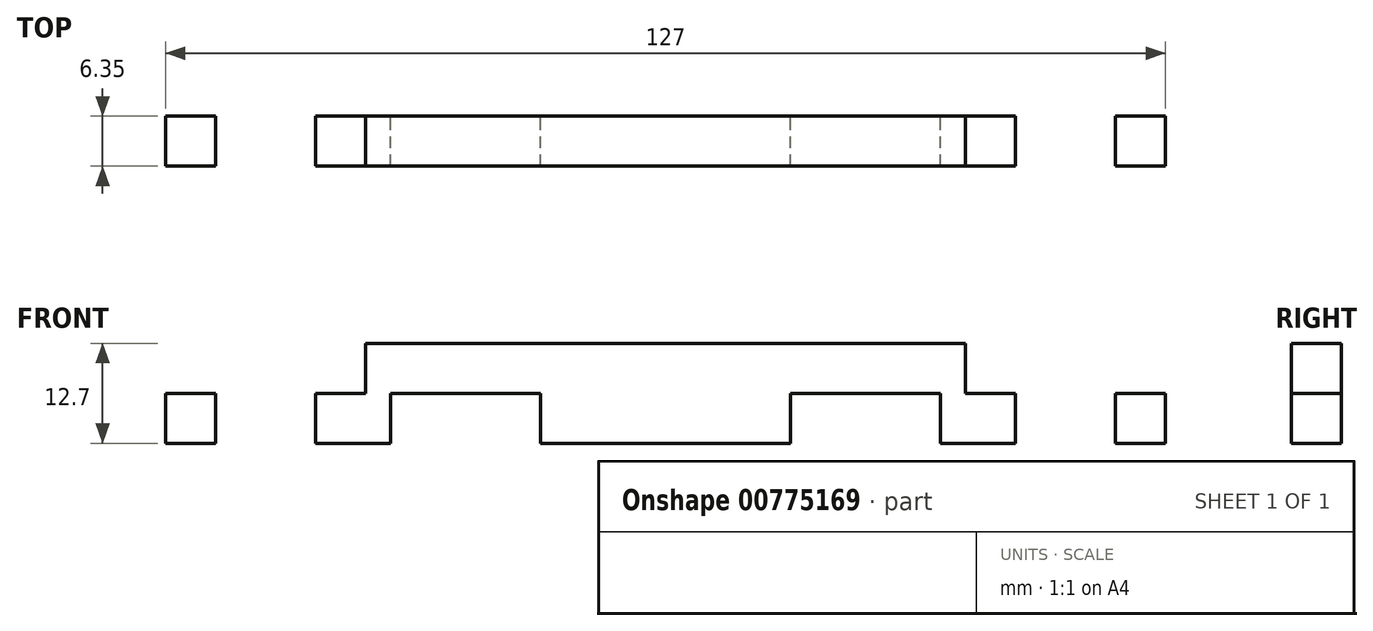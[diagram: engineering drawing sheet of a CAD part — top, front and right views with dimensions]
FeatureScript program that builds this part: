
annotation { "Feature Type Name" : "Feature", "Feature Type Description" : "" }
export const myFeature = defineFeature(function(context is Context, id is Id, definition is map)
    precondition{}
    {
        {
            var Q0;
            Q0=qCreatedBy(makeId("Front.planeOp"),FACE);
            var sketch = newSketch(context, id + "F0", { "sketchPlane" : qUnion([Q0])});
            skLineSegment(sketch, "E0.bottom", {"start": v(63.5, 9.52) * mm, "end": v(-63.5, 9.52) * mm});
            skLineSegment(sketch, "E0.top", {"start": v(63.5, -9.52) * mm, "end": v(-63.5, -9.53) * mm});
            skLineSegment(sketch, "E0.left", {"start": v(63.5, 9.53) * mm, "end": v(63.5, -9.52) * mm});
            skLineSegment(sketch, "E0.right", {"start": v(-63.5, 9.52) * mm, "end": v(-63.5, -9.53) * mm});
            skPoint(sketch, "E0.middle", {"position": v(0, 0) * mm});
            skLineSegment(sketch, "E1.bottom", {"start": v(-63.5, 9.52) * mm, "end": v(-57.15, 9.52) * mm});
            skLineSegment(sketch, "E1.top", {"start": v(-63.5, -9.53) * mm, "end": v(-57.15, -9.53) * mm});
            skLineSegment(sketch, "E1.right", {"start": v(-57.15, 9.53) * mm, "end": v(-57.15, -9.53) * mm});
            skLineSegment(sketch, "E2.bottom", {"start": v(-44.45, 9.52) * mm, "end": v(-38.1, 9.52) * mm});
            skLineSegment(sketch, "E2.top", {"start": v(-44.45, -9.53) * mm, "end": v(-38.1, -9.53) * mm});
            skLineSegment(sketch, "E2.left", {"start": v(-44.45, 9.53) * mm, "end": v(-44.45, -9.53) * mm});
            skLineSegment(sketch, "E2.right", {"start": v(-38.1, 9.53) * mm, "end": v(-38.1, -9.53) * mm});
            skLineSegment(sketch, "E3.bottom", {"start": v(-57.15, 3.17) * mm, "end": v(-63.5, 3.17) * mm});
            skLineSegment(sketch, "E3.top", {"start": v(-57.15, -3.18) * mm, "end": v(-63.5, -3.18) * mm});
            skLineSegment(sketch, "E3.left", {"start": v(-57.15, 3.18) * mm, "end": v(-57.15, -3.18) * mm});
            skLineSegment(sketch, "E3.right", {"start": v(-63.5, 3.18) * mm, "end": v(-63.5, -3.18) * mm});
            skPoint(sketch, "E3.middle", {"position": v(-60.33, 0) * mm});
            skPoint(sketch, "E3.middle.positionSnap0", {"position": v(-60.33, 9.52) * mm});
            skPoint(sketch, "E3.middle.positionSnap1", {"position": v(-63.5, 0) * mm});
            skPoint(sketch, "E3.centerSnap0", {"position": v(-60.33, 9.52) * mm});
            skPoint(sketch, "E3.centerSnap1", {"position": v(-63.5, 0) * mm});
            skLineSegment(sketch, "E4.bottom", {"start": v(-38.1, 3.17) * mm, "end": v(-44.45, 3.17) * mm});
            skLineSegment(sketch, "E4.top", {"start": v(-38.1, -3.17) * mm, "end": v(-44.45, -3.17) * mm});
            skLineSegment(sketch, "E4.left", {"start": v(-38.1, 3.18) * mm, "end": v(-38.1, -3.18) * mm});
            skLineSegment(sketch, "E4.right", {"start": v(-44.45, 3.18) * mm, "end": v(-44.45, -3.18) * mm});
            skPoint(sketch, "E4.middle", {"position": v(-41.28, 0) * mm});
            skPoint(sketch, "E4.middle.positionSnap0", {"position": v(-41.28, 9.53) * mm});
            skPoint(sketch, "E4.centerSnap0", {"position": v(-41.28, 9.53) * mm});
            skLineSegment(sketch, "E5.MirrorCS", {"start": v(63.5, 9.52) * mm, "end": v(57.15, 9.52) * mm});
            skLineSegment(sketch, "E6.MirrorCS", {"start": v(63.5, 3.18) * mm, "end": v(63.5, -3.18) * mm});
            skLineSegment(sketch, "E7.MirrorCS", {"start": v(44.45, 9.52) * mm, "end": v(38.1, 9.52) * mm});
            skPoint(sketch, "E8.MirrorP", {"position": v(60.33, 9.52) * mm});
            skLineSegment(sketch, "E9.MirrorCS", {"start": v(44.45, 3.18) * mm, "end": v(44.45, -3.18) * mm});
            skLineSegment(sketch, "E10.MirrorCS", {"start": v(63.5, 9.52) * mm, "end": v(63.5, -9.53) * mm});
            skPoint(sketch, "E11.MirrorP", {"position": v(63.5, 0) * mm});
            skLineSegment(sketch, "E12.MirrorCS", {"start": v(38.1, 3.18) * mm, "end": v(38.1, -3.18) * mm});
            skPoint(sketch, "E13.MirrorP", {"position": v(41.28, 9.53) * mm});
            skPoint(sketch, "E14.MirrorP", {"position": v(60.33, 0) * mm});
            skLineSegment(sketch, "E15.MirrorCS", {"start": v(57.15, -3.18) * mm, "end": v(63.5, -3.18) * mm});
            skPoint(sketch, "E16.MirrorP", {"position": v(41.28, 0) * mm});
            skLineSegment(sketch, "E17.MirrorCS", {"start": v(44.45, -9.53) * mm, "end": v(38.1, -9.53) * mm});
            skLineSegment(sketch, "E18.MirrorCS", {"start": v(57.15, 9.53) * mm, "end": v(57.15, -9.53) * mm});
            skLineSegment(sketch, "E19.MirrorCS", {"start": v(63.5, -9.53) * mm, "end": v(57.15, -9.53) * mm});
            skLineSegment(sketch, "E20.MirrorCS", {"start": v(38.1, -3.17) * mm, "end": v(44.45, -3.17) * mm});
            skLineSegment(sketch, "E21.MirrorCS", {"start": v(44.45, 9.53) * mm, "end": v(44.45, -9.53) * mm});
            skLineSegment(sketch, "E22.MirrorCS", {"start": v(38.1, 3.17) * mm, "end": v(44.45, 3.17) * mm});
            skLineSegment(sketch, "E23.MirrorCS", {"start": v(57.15, 3.18) * mm, "end": v(57.15, -3.18) * mm});
            skLineSegment(sketch, "E24.MirrorCS", {"start": v(38.1, 9.53) * mm, "end": v(38.1, -9.53) * mm});
            skLineSegment(sketch, "E25.MirrorCS", {"start": v(57.15, 3.17) * mm, "end": v(63.5, 3.17) * mm});
            skLineSegment(sketch, "E26", {"start": v(-57.15, -3.18) * mm, "end": v(57.15, -3.18) * mm});
            skLineSegment(sketch, "E27.bottom", {"start": v(-38.1, -9.53) * mm, "end": v(-25.4, -9.53) * mm});
            skLineSegment(sketch, "E27.top", {"start": v(-38.1, -3.18) * mm, "end": v(-25.4, -3.18) * mm});
            skLineSegment(sketch, "E27.left", {"start": v(-38.1, -9.53) * mm, "end": v(-38.1, -3.18) * mm});
            skLineSegment(sketch, "E27.right", {"start": v(-25.4, -9.53) * mm, "end": v(-25.4, -3.18) * mm});
            skLineSegment(sketch, "E28.bottom", {"start": v(-12.7, -9.53) * mm, "end": v(0, -9.53) * mm});
            skLineSegment(sketch, "E28.top", {"start": v(-12.7, -3.18) * mm, "end": v(0, -3.18) * mm});
            skLineSegment(sketch, "E28.left", {"start": v(-12.7, -9.53) * mm, "end": v(-12.7, -3.18) * mm});
            skLineSegment(sketch, "E28.right", {"start": v(0, -9.53) * mm, "end": v(0, -3.18) * mm});
            skLineSegment(sketch, "E29.bottom", {"start": v(12.7, -9.52) * mm, "end": v(25.4, -9.52) * mm});
            skLineSegment(sketch, "E29.top", {"start": v(12.7, -3.18) * mm, "end": v(25.4, -3.18) * mm});
            skLineSegment(sketch, "E29.left", {"start": v(12.7, -9.53) * mm, "end": v(12.7, -3.18) * mm});
            skLineSegment(sketch, "E29.right", {"start": v(25.4, -9.53) * mm, "end": v(25.4, -3.18) * mm});
            skLineSegment(sketch, "E30.top", {"start": v(-38.1, -3.18) * mm, "end": v(-19.05, -3.18) * mm});
            skLineSegment(sketch, "E30.left", {"start": v(-38.1, 3.17) * mm, "end": v(-38.1, -3.18) * mm});
            skLineSegment(sketch, "E31.top", {"start": v(38.1, -3.18) * mm, "end": v(19.05, -3.18) * mm});
            skLineSegment(sketch, "E32.bottom", {"start": v(15.88, -3.18) * mm, "end": v(34.93, -3.18) * mm});
            skLineSegment(sketch, "E32.top", {"start": v(15.88, 3.18) * mm, "end": v(34.93, 3.18) * mm});
            skLineSegment(sketch, "E32.left", {"start": v(15.88, -3.18) * mm, "end": v(15.88, 3.18) * mm});
            skLineSegment(sketch, "E32.right", {"start": v(34.93, -3.18) * mm, "end": v(34.93, 3.18) * mm});
            skLineSegment(sketch, "E33.bottom", {"start": v(-15.88, -3.18) * mm, "end": v(-34.93, -3.18) * mm});
            skLineSegment(sketch, "E33.top", {"start": v(-15.88, 3.17) * mm, "end": v(-34.93, 3.17) * mm});
            skLineSegment(sketch, "E33.left", {"start": v(-15.88, -3.18) * mm, "end": v(-15.88, 3.18) * mm});
            skLineSegment(sketch, "E33.right", {"start": v(-34.93, -3.18) * mm, "end": v(-34.93, 3.18) * mm});
            skSolve(sketch);
        }
        {
            var Q0;
            Q0=makeQuery(id+"F0.imprint","IMPRINT",FACE,{"disambiguationData":[TD([[makeQuery(id+"F0.imprint","IMPRINT",EDGE,{"derivedFrom":sQuery(id+"F0.wireOp",EDGE,"LQrqsIvc-0tii-S9FF-bkIL-ofT4X19JhIAi.bottom")}),1.0]])]});
            var Q1;
            {var subQ3=sQuery(id+"F0.wireOp",EDGE,"E4.left");Q1=makeQuery(id+"F0.imprint","IMPRINT",FACE,{"disambiguationData":[TD([[makeQuery(id+"F0.imprint","IMPRINT",EDGE,{"derivedFrom":subQ3}),1.0]])]});}
            var Q2;
            {var subQ3=sQuery(id+"F0.wireOp",EDGE,"E3.left");Q2=makeQuery(id+"F0.imprint","IMPRINT",FACE,{"disambiguationData":[TD([[makeQuery(id+"F0.imprint","IMPRINT",EDGE,{"derivedFrom":subQ3}),1.0]])]});}
            var Q3;
            Q3=makeQuery(id+"F0.imprint","IMPRINT",FACE,{"disambiguationData":[TD([[makeQuery(id+"F0.imprint","IMPRINT",EDGE,{"derivedFrom":sQuery(id+"F0.wireOp",EDGE,"E3.bottom")}),1.0]])]});
            var Q4;
            Q4=makeQuery(id+"F0.imprint","IMPRINT",FACE,{"disambiguationData":[TD([[makeQuery(id+"F0.imprint","IMPRINT",EDGE,{"derivedFrom":sQuery(id+"F0.wireOp",EDGE,"E4.bottom")}),1.0]])]});
            var Q5;
            {var subQ0=sQuery(id+"F0.wireOp",EDGE,"E20.MirrorCS");Q5=makeQuery(id+"F0.imprint","IMPRINT",FACE,{"disambiguationData":[TD([[makeQuery(id+"F0.imprint","IMPRINT",EDGE,{"derivedFrom":subQ0}),1.0]])]});}
            var Q6;
            {var subQ0=sQuery(id+"F0.wireOp",EDGE,"E15.MirrorCS");Q6=makeQuery(id+"F0.imprint","IMPRINT",FACE,{"disambiguationData":[TD([[makeQuery(id+"F0.imprint","IMPRINT",EDGE,{"derivedFrom":subQ0}),1.0]])]});}
            var Q7;
            {var subQ3=sQuery(id+"F0.wireOp",EDGE,"E23.MirrorCS");Q7=makeQuery(id+"F0.imprint","IMPRINT",FACE,{"disambiguationData":[TD([[makeQuery(id+"F0.imprint","IMPRINT",EDGE,{"derivedFrom":subQ3}),-1.0]])]});}
            var Q8;
            {var subQ0=sQuery(id+"F0.wireOp",EDGE,"E22.MirrorCS");Q8=makeQuery(id+"F0.imprint","IMPRINT",FACE,{"disambiguationData":[TD([[makeQuery(id+"F0.imprint","IMPRINT",EDGE,{"derivedFrom":subQ0}),-1.0]])]});}
            var Q9;
            Q9=makeQuery(id+"F0.imprint","IMPRINT",FACE,{"disambiguationData":[TD([[makeQuery(id+"F0.imprint","IMPRINT",EDGE,{"derivedFrom":sQuery(id+"F0.wireOp",EDGE,"E27.bottom")}),1.0]])]});
            var Q10;
            Q10=makeQuery(id+"F0.imprint","IMPRINT",FACE,{"disambiguationData":[TD([[makeQuery(id+"F0.imprint","IMPRINT",EDGE,{"derivedFrom":sQuery(id+"F0.wireOp",EDGE,"E28.bottom")}),1.0]])]});
            var Q11;
            Q11=makeQuery(id+"F0.imprint","IMPRINT",FACE,{"disambiguationData":[TD([[makeQuery(id+"F0.imprint","IMPRINT",EDGE,{"derivedFrom":sQuery(id+"F0.wireOp",EDGE,"E29.bottom")}),1.0]])]});
            var Q12;
            {var subQ2=sQuery(id+"F0.wireOp",EDGE,"E2.right");Q12=makeQuery(id+"F0.imprint","IMPRINT",FACE,{"disambiguationData":[TD([[makeQuery(id+"F0.imprint","IMPRINT",EDGE,{"derivedFrom":subQ2}),1.0]])]});}
            extrude(context, id + "F1", {"entities" : qUnion([Q0, Q1, Q2, Q3, Q4, Q5, Q6, Q7, Q8, Q9, Q10, Q11, Q12]), "depth" : 6.35 * mm, "offsetDistance" : 25.4 * mm});
        }
    });
